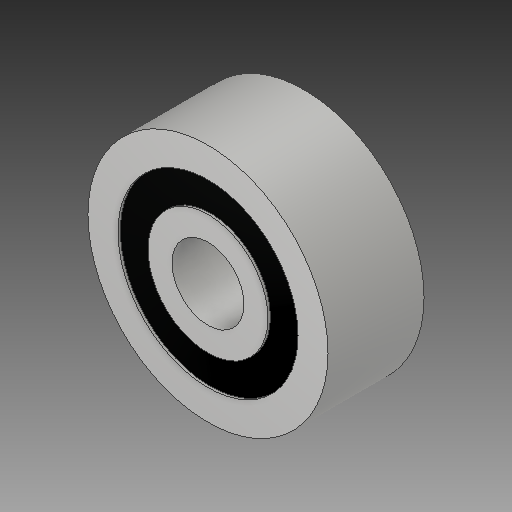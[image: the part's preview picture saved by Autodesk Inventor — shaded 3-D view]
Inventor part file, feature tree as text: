
AUTODESK INVENTOR PART (.ipt)
format: ipt  version: 2018 (Build 220112000, 112)  size: 139,776 bytes
history: native  units: in
note: dims shown in document units (in); Inventor stores cm internally (conversion verified against a paired STEP export)
features: extrude x2, sketch x2, mirror x1, projected_geometry x1
ambient origin geometry x8: Origin, YZ Plane, XZ Plane, XY Plane, X Axis, Y Axis, Z Axis, Center Point
bodies: Solid1 (feature_tree)
feature tree (6):
  extrude  "Extrusion1"  Depth=0.3937in
  extrude  "Extrusion2"  Depth=0.0039in
  mirror  "Mirror1"
  sketch  "Sketch1"  dims[d0=0.1181in d1=0.3937in]
  sketch  "Sketch2"  dims[d2=0.1575in d3=0.0in d4=0.0492in d5=0.0394in d6=0.0039in d7=0.0in]
  projected_geometry  "Projected Loop1"
